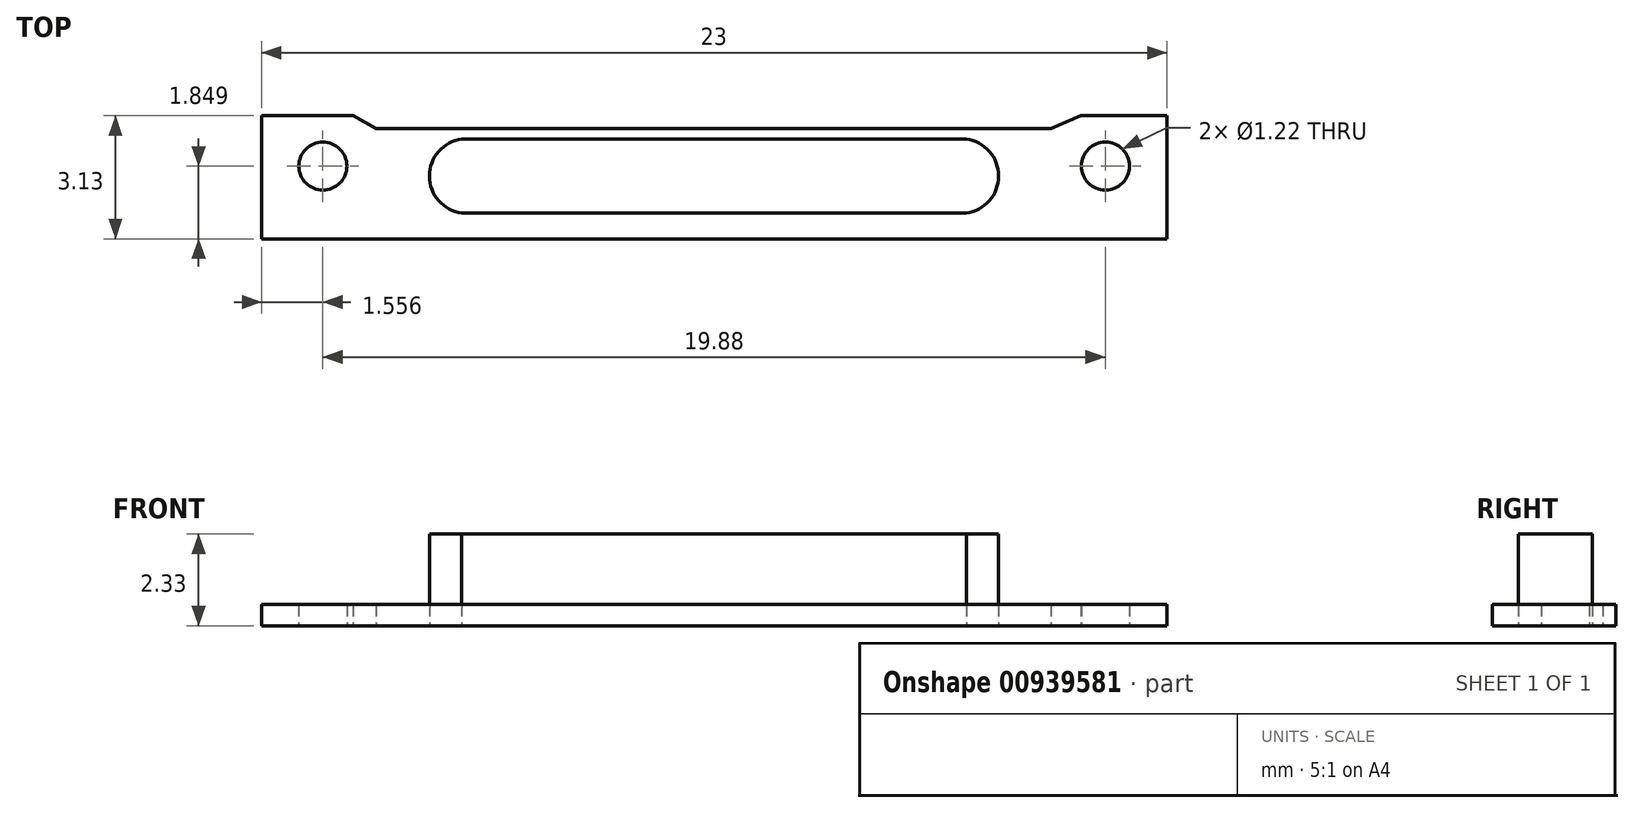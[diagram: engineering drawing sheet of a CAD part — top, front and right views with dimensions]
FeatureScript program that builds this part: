
annotation { "Feature Type Name" : "Feature", "Feature Type Description" : "" }
export const myFeature = defineFeature(function(context is Context, id is Id, definition is map)
    precondition{}
    {
        {
            var Q0;
            Q0=qCreatedBy(makeId("Top.planeOp"),FACE);
            var sketch = newSketch(context, id + "F0", { "sketchPlane" : qUnion([Q0])});
            skLineSegment(sketch, "E0.bottom", {"start": v(-24.68, 7.67) * mm, "end": v(-1.68, 7.67) * mm});
            skLineSegment(sketch, "E0.top", {"start": v(-24.68, 4.54) * mm, "end": v(-1.68, 4.54) * mm});
            skLineSegment(sketch, "E0.left", {"start": v(-24.68, 7.67) * mm, "end": v(-24.68, 4.54) * mm});
            skLineSegment(sketch, "E0.right", {"start": v(-1.68, 7.67) * mm, "end": v(-1.68, 4.54) * mm});
            skSolve(sketch);
        }
        {
            var Q0;
            Q0=qCreatedBy(makeId("Top.planeOp"),FACE);
            var sketch = newSketch(context, id + "F1", { "sketchPlane" : qUnion([Q0])});
            skCircle(sketch, "E1", {"center": v(-23.12, 6.39) * mm, "radius": 0.61 * mm});
            skCircle(sketch, "E2", {"center": v(-3.24, 6.39) * mm, "radius": 0.61 * mm});
            skSolve(sketch);
        }
        {
            var Q0;
            Q0 = qSketchRegion(id + "F0", true);
            var Q1;
            Q1 = qSketchRegion(id + "F4", true);
            extrude(context, id + "F2", {"entities" : qUnion([Q0, Q1]), "depth" : 0.54 * mm, "offsetDistance" : 25 * mm});
        }
        {
            var Q0;
            Q0 = qSketchRegion(id + "F1", true);
            extrude(context, id + "F3", {"entities" : qUnion([Q0]), "operationType" : NewBodyOperationType.REMOVE, "depth" : 0.54 * mm, "offsetDistance" : 25 * mm});
        }
        {
            var Q0;
            Q0=qCreatedBy(makeId("Top.planeOp"),FACE);
            var sketch = newSketch(context, id + "F4", { "sketchPlane" : qUnion([Q0])});
            skLineSegment(sketch, "E3.bottom", {"start": v(-19.6, 5.2) * mm, "end": v(-6.78, 5.2) * mm});
            skLineSegment(sketch, "E3.top", {"start": v(-19.6, 7.08) * mm, "end": v(-6.78, 7.08) * mm});
            skArc(sketch, "E4", {"start": v(-20.42, 6.14) * mm, "mid": v(-20.18, 5.51) * mm, "end": v(-19.6, 5.2) * mm});
            skArc(sketch, "E5.MirrorCS", {"start": v(-20.42, 6.14) * mm, "mid": v(-20.18, 6.76) * mm, "end": v(-19.6, 7.08) * mm});
            skArc(sketch, "E6.MirrorCS", {"start": v(-5.96, 6.14) * mm, "mid": v(-6.2, 6.76) * mm, "end": v(-6.78, 7.08) * mm});
            skArc(sketch, "E7.MirrorCS", {"start": v(-5.96, 6.14) * mm, "mid": v(-6.2, 5.51) * mm, "end": v(-6.78, 5.2) * mm});
            skSolve(sketch);
        }
        {
            var Q0;
            Q0 = qSketchRegion(id + "F4", true);
            extrude(context, id + "F5", {"entities" : qUnion([Q0]), "depth" : 2.33 * mm, "offsetDistance" : 25 * mm});
        }
        {
            var Q0;
            Q0=qCreatedBy(makeId("Top.planeOp"),FACE);
            var sketch = newSketch(context, id + "F6", { "sketchPlane" : qUnion([Q0])});
            skLineSegment(sketch, "E8.bottom", {"start": v(-22.47, 8.11) * mm, "end": v(-3.73, 8.11) * mm});
            skLineSegment(sketch, "E8.top", {"start": v(-21.77, 7.34) * mm, "end": v(-4.62, 7.34) * mm});
            skLineSegment(sketch, "E8.left", {"start": v(-22.47, 8.11) * mm, "end": v(-22.47, 7.73) * mm});
            skLineSegment(sketch, "E8.right", {"start": v(-3.73, 8.11) * mm, "end": v(-3.73, 7.73) * mm});
            skLineSegment(sketch, "E9", {"start": v(-22.47, 7.73) * mm, "end": v(-21.77, 7.34) * mm});
            skLineSegment(sketch, "E10", {"start": v(-3.73, 7.73) * mm, "end": v(-4.62, 7.34) * mm});
            skSolve(sketch);
        }
        {
            var Q0;
            Q0 = qSketchRegion(id + "F6", true);
            extrude(context, id + "F7", {"entities" : qUnion([Q0]), "operationType" : NewBodyOperationType.REMOVE, "depth" : 25 * mm, "offsetDistance" : 25 * mm});
        }
    });
